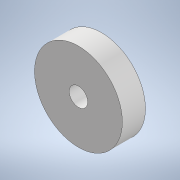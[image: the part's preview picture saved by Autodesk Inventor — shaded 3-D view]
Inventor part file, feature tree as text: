
AUTODESK INVENTOR PART (.ipt)
format: ipt  version: 2020 (Build 240168000, 168)  size: 98,304 bytes
history: native  units: mm
features: other x3, extrude x1, sketch x1, reference x1
ambient origin geometry x8: Origin, YZ Plane, XZ Plane, XY Plane, X Axis, Y Axis, Z Axis, Center Point
bodies: Solid1 (feature_tree)
feature tree (6):
  extrude  "Extrusion1"  Depth=2.5mm
  sketch  "Sketch1"  dims[d0=2.0mm d1=9.5mm d2=2.5mm d3=0.0mm]
  reference  "Reference1"
  parser-record x1  (decoder bookkeeping rows leaked as tree rows — omitted from the tree; the rows remain in map.json)
  other  "reducer_1_MIR.iam"
  other  "tendon_wh_1_MIR:1"
note: 1 file-system path scrubbed to <path> (originals preserved in map.json)
